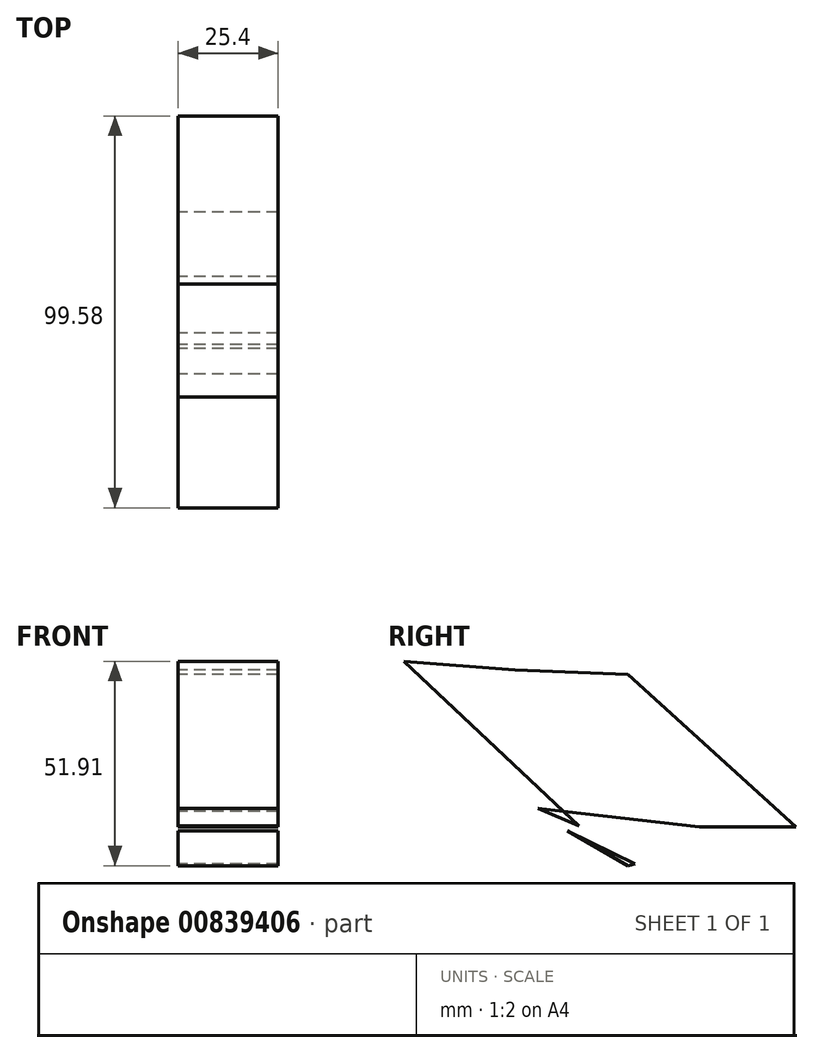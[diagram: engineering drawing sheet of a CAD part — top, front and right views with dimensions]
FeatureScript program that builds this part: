
annotation { "Feature Type Name" : "Feature", "Feature Type Description" : "" }
export const myFeature = defineFeature(function(context is Context, id is Id, definition is map)
    precondition{}
    {
        {
            var Q0;
            Q0=qCreatedBy(makeId("Right.planeOp"),FACE);
            var sketch = newSketch(context, id + "F0", { "sketchPlane" : qUnion([Q0])});
            skLineSegment(sketch, "E0", {"start": v(-28.63, 20.78) * mm, "end": v(18.26, -19.19) * mm});
            skLineSegment(sketch, "E1", {"start": v(18.26, -19.19) * mm, "end": v(42.74, -19.19) * mm});
            skLineSegment(sketch, "E2", {"start": v(42.74, -19.19) * mm, "end": v(0, 19.61) * mm});
            skLineSegment(sketch, "E3", {"start": v(0, 19.61) * mm, "end": v(-28.63, 20.78) * mm});
            skLineSegment(sketch, "E4", {"start": v(-56.84, 22.91) * mm, "end": v(-28.63, 20.78) * mm});
            skLineSegment(sketch, "E5", {"start": v(-12.45, -18.93) * mm, "end": v(-56.84, 22.91) * mm});
            skLineSegment(sketch, "E6", {"start": v(18.26, -19.19) * mm, "end": v(-22.82, -14.46) * mm});
            skLineSegment(sketch, "E7", {"start": v(-22.82, -14.46) * mm, "end": v(-12.45, -18.93) * mm});
            skLineSegment(sketch, "E8", {"start": v(36.1, -42.48) * mm, "end": v(52.7, -41.2) * mm});
            skLineSegment(sketch, "E9", {"start": v(52.7, -41.2) * mm, "end": v(43.15, -18.22) * mm});
            skLineSegment(sketch, "E10", {"start": v(43.15, -18.22) * mm, "end": v(0, -29) * mm});
            skLineSegment(sketch, "E11", {"start": v(0, -29) * mm, "end": v(-15.35, -20.11) * mm});
            skLineSegment(sketch, "E12", {"start": v(-15.35, -20.11) * mm, "end": v(28.63, -41.62) * mm});
            skLineSegment(sketch, "E13", {"start": v(28.63, -41.62) * mm, "end": v(36.51, -39.58) * mm});
            skSolve(sketch);
        }
        {
            var Q0;
            Q0 = qSketchRegion(id + "F0", true);
            extrude(context, id + "F1", {"entities" : qUnion([Q0]), "depth" : 25.4 * mm, "offsetDistance" : 25.4 * mm});
        }
    });
